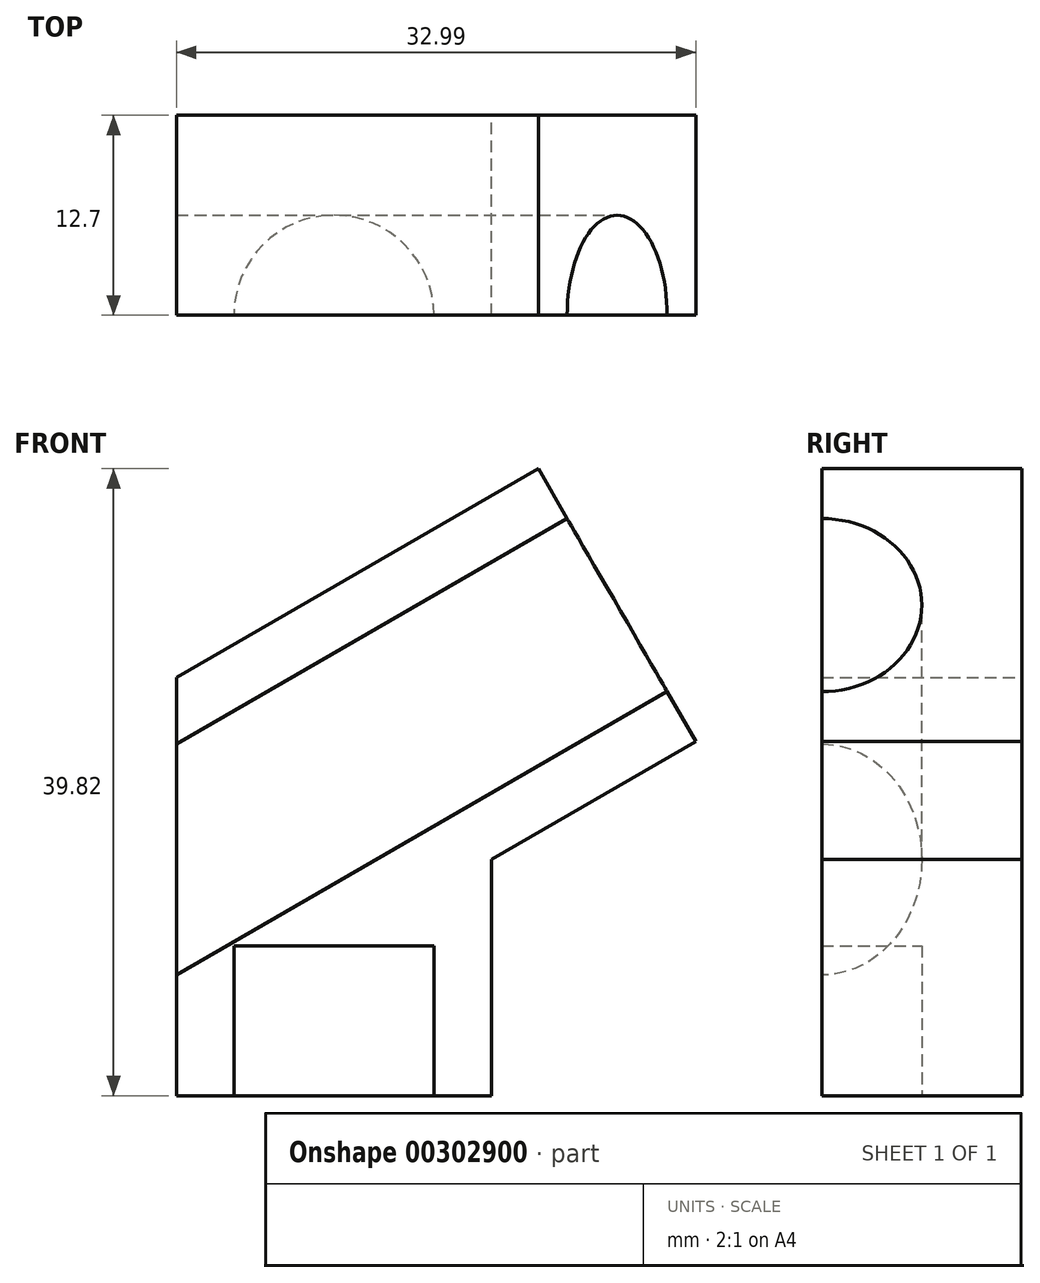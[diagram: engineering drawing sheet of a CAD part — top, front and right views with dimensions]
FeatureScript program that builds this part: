
annotation { "Feature Type Name" : "Feature", "Feature Type Description" : "" }
export const myFeature = defineFeature(function(context is Context, id is Id, definition is map)
    precondition{}
    {
        {
            var Q0;
            Q0=qCreatedBy(makeId("Front.planeOp"),FACE);
            var sketch = newSketch(context, id + "F0", { "sketchPlane" : qUnion([Q0])});
            skLineSegment(sketch, "E0", {"start": v(-20, -15) * mm, "end": v(-20, 11.55) * mm});
            skLineSegment(sketch, "E1", {"start": v(-20, 11.55) * mm, "end": v(3, 24.82) * mm});
            skLineSegment(sketch, "E2", {"start": v(3, 24.82) * mm, "end": v(13, 7.5) * mm});
            skLineSegment(sketch, "E3", {"start": v(13, 7.5) * mm, "end": v(0, 0) * mm});
            skLineSegment(sketch, "E4", {"start": v(0, 0) * mm, "end": v(0, -15) * mm});
            skLineSegment(sketch, "E5", {"start": v(0, -15) * mm, "end": v(-20, -15) * mm});
            skLineSegment(sketch, "E6", {"start": v(-20, -15) * mm, "end": v(-20, -15) * mm});
            skSolve(sketch);
        }
        {
            var Q0;
            Q0 = qSketchRegion(id + "F0", true);
            extrude(context, id + "F1", {"entities" : qUnion([Q0]), "depth" : 12.7 * mm});
        }
        {
            var Q0;
            Q0=makeQuery(id+"F1.opExtrude","SWEPT_FACE",FACE,{"disambiguationData":[OSD([sQuery(id+"F0.wireOp",EDGE,"E2")])]});
            var sketch = newSketch(context, id + "F2", { "sketchPlane" : qUnion([Q0])});
            skCircle(sketch, "E7", {"center": v(-12.7, 10) * mm, "radius": 6.35 * mm});
            skSolve(sketch);
        }
        {
            var Q0;
            Q0 = qSketchRegion(id + "F2", true);
            extrude(context, id + "F3", {"entities" : qUnion([Q0]), "operationType" : NewBodyOperationType.REMOVE, "endBound" : BoundingType.THROUGH_ALL, "oppositeDirection" : true, "depth" : 9.52 * mm});
        }
        {
            var Q0;
            Q0=makeQuery(id+"F1.opExtrude","SWEPT_FACE",FACE,{"disambiguationData":[OSD([sQuery(id+"F0.wireOp",EDGE,"E5")])]});
            var sketch = newSketch(context, id + "F4", { "sketchPlane" : qUnion([Q0])});
            skCircle(sketch, "E8", {"center": v(-10, 12.7) * mm, "radius": 6.35 * mm});
            skSolve(sketch);
        }
        {
            var Q0;
            Q0 = qSketchRegion(id + "F4", true);
            extrude(context, id + "F5", {"entities" : qUnion([Q0]), "operationType" : NewBodyOperationType.REMOVE, "oppositeDirection" : true, "depth" : 9.52 * mm});
        }
    });
